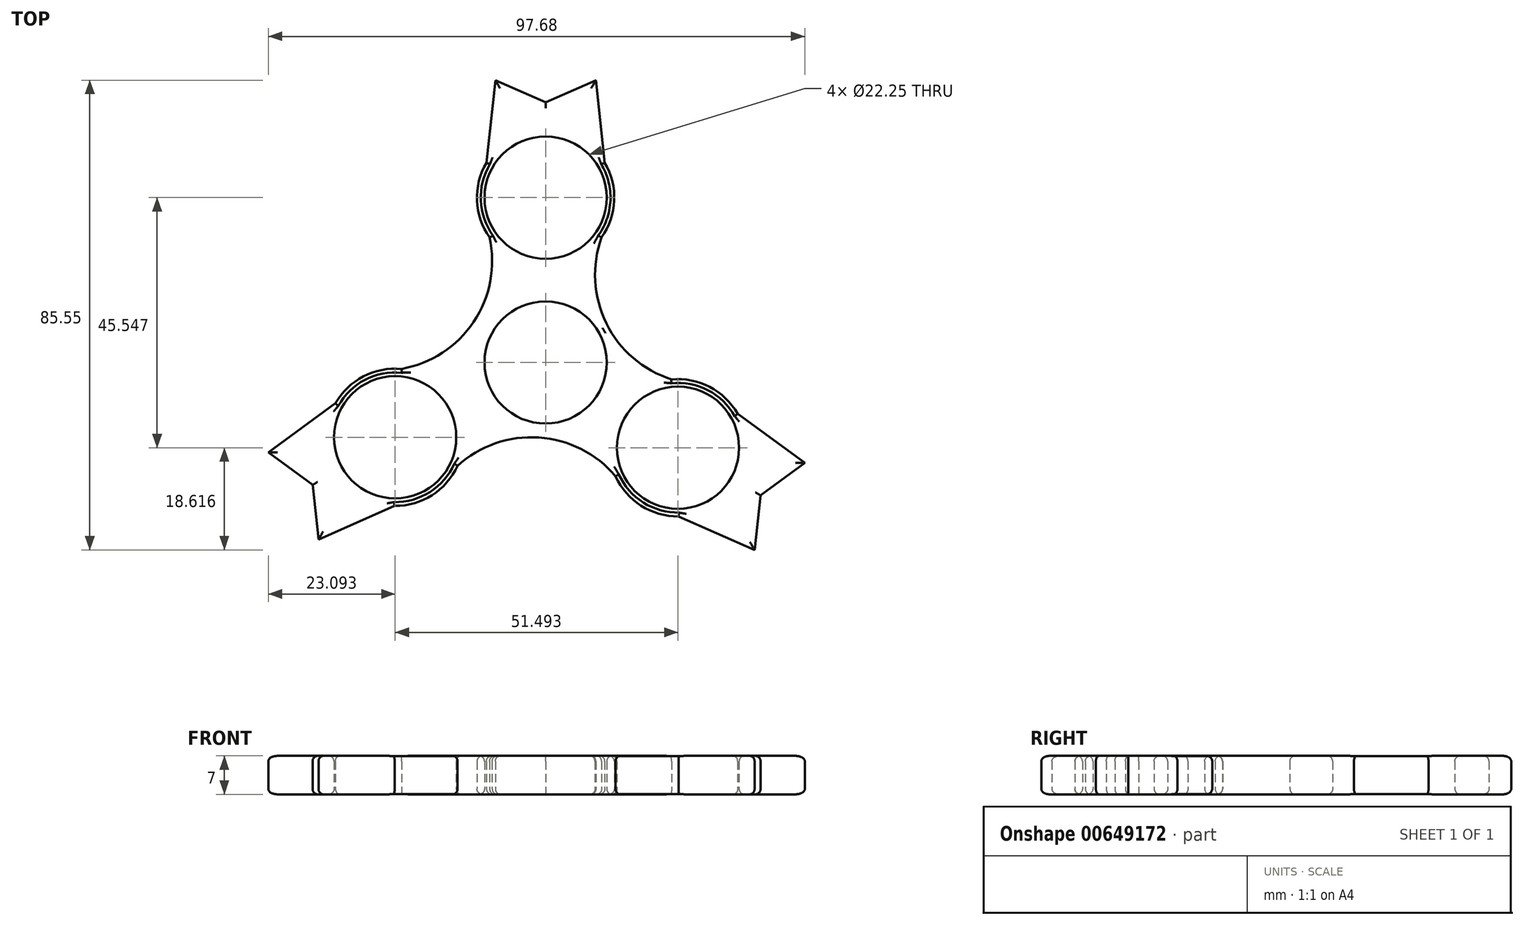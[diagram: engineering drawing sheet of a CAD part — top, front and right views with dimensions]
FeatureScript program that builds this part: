
annotation { "Feature Type Name" : "Feature", "Feature Type Description" : "" }
export const myFeature = defineFeature(function(context is Context, id is Id, definition is map)
    precondition{}
    {
        {
            var Q0;
            Q0=qCreatedBy(makeId("Top.planeOp"),FACE);
            var sketch = newSketch(context, id + "F0", { "sketchPlane" : qUnion([Q0])});
            skCircle(sketch, "E0", {"center": v(0, 0) * mm, "radius": 11.13 * mm});
            skLineSegment(sketch, "E1", {"start": v(32.45, -16.12) * mm, "end": v(32.45, -21.33) * mm, "construction": true});
            skLineSegment(sketch, "E2", {"start": v(-9.15, 36.82) * mm, "end": v(9.15, 36.82) * mm, "construction": true});
            skLineSegment(sketch, "E3", {"start": v(-10.78, 36.35) * mm, "end": v(-9.15, 51.4) * mm});
            skLineSegment(sketch, "E4", {"start": v(-9.15, 51.4) * mm, "end": v(0, 47.38) * mm});
            skLineSegment(sketch, "E5", {"start": v(0, 47.38) * mm, "end": v(9.15, 51.4) * mm});
            skLineSegment(sketch, "E6", {"start": v(9.15, 51.4) * mm, "end": v(10.78, 36.35) * mm});
            skCircle(sketch, "E7", {"center": v(0, 30.02) * mm, "radius": 11.13 * mm});
            skLineSegment(sketch, "E8", {"start": v(-11.33, 31.25) * mm, "end": v(11.33, 31.25) * mm, "construction": true});
            skArc(sketch, "E9", {"start": v(-10.78, 36.35) * mm, "mid": v(-12.49, 29.48) * mm, "end": v(-10.19, 22.78) * mm});
            skCircle(sketch, "E10.1.0", {"center": v(-27.4, -13.62) * mm, "radius": 11.13 * mm});
            skLineSegment(sketch, "E10.1.1", {"start": v(-50.5, -16.38) * mm, "end": v(-38.27, -7.45) * mm});
            skLineSegment(sketch, "E10.1.2", {"start": v(-42.43, -22.3) * mm, "end": v(-50.5, -16.38) * mm});
            skLineSegment(sketch, "E10.1.3", {"start": v(-41.34, -32.24) * mm, "end": v(-42.43, -22.3) * mm});
            skLineSegment(sketch, "E10.1.4", {"start": v(-27.49, -26.12) * mm, "end": v(-41.34, -32.24) * mm});
            skArc(sketch, "E10.1.5", {"start": v(-27.49, -26.12) * mm, "mid": v(-20.68, -24.16) * mm, "end": v(-16.03, -18.82) * mm});
            skCircle(sketch, "E10.2.0", {"center": v(24.1, -15.52) * mm, "radius": 11.13 * mm});
            skLineSegment(sketch, "E10.2.1", {"start": v(38.04, -34.14) * mm, "end": v(24.19, -28.02) * mm});
            skLineSegment(sketch, "E10.2.2", {"start": v(39.13, -24.2) * mm, "end": v(38.04, -34.14) * mm});
            skLineSegment(sketch, "E10.2.3", {"start": v(47.2, -18.29) * mm, "end": v(39.13, -24.2) * mm});
            skLineSegment(sketch, "E10.2.4", {"start": v(34.97, -9.35) * mm, "end": v(47.2, -18.29) * mm});
            skArc(sketch, "E10.2.5", {"start": v(34.97, -9.35) * mm, "mid": v(13.27, -9.27) * mm, "end": v(24.19, -28.02) * mm});
            skPoint(sketch, "E10.center", {"position": v(-1.1, 0.3) * mm});
            skArc(sketch, "E11", {"start": v(12.73, -20.73) * mm, "mid": v(-1.24, -13.65) * mm, "end": v(-16.03, -18.82) * mm});
            skLineSegment(sketch, "E12", {"start": v(-16.03, -18.82) * mm, "end": v(-27.49, -26.12) * mm, "construction": true});
            skLineSegment(sketch, "E13", {"start": v(12.73, -20.73) * mm, "end": v(24.19, -28.02) * mm, "construction": true});
            skArc(sketch, "E14", {"start": v(10.19, 22.78) * mm, "mid": v(11.05, 7.14) * mm, "end": v(22.92, -3.08) * mm});
            skArc(sketch, "E15", {"start": v(-26.22, -1.17) * mm, "mid": v(-13.1, 7.4) * mm, "end": v(-10.19, 22.78) * mm});
            skLineSegment(sketch, "E16", {"start": v(-26.22, -1.17) * mm, "end": v(-38.27, -7.45) * mm, "construction": true});
            skLineSegment(sketch, "E17", {"start": v(-10.3, 25.12) * mm, "end": v(-10.32, 25.88) * mm, "construction": true});
            skLineSegment(sketch, "E18", {"start": v(10.19, 22.78) * mm, "end": v(10.78, 36.35) * mm, "construction": true});
            skLineSegment(sketch, "E19.trimOffspring", {"start": v(-10.56, 31.25) * mm, "end": v(-10.78, 36.35) * mm, "construction": true});
            skArc(sketch, "E20.trimOffspring", {"start": v(10.19, 22.78) * mm, "mid": v(12.49, 29.48) * mm, "end": v(10.78, 36.35) * mm});
            skArc(sketch, "E21.trimOffspring", {"start": v(-26.22, -1.17) * mm, "mid": v(-33.17, -2.53) * mm, "end": v(-38.27, -7.45) * mm});
            skSolve(sketch);
        }
        {
            var Q0;
            Q0=qSketchRegion(id+"F0",true);
            extrude(context, id + "F1", {"entities" : qUnion([Q0]), "depth" : 7 * mm, "offsetDistance" : 25 * mm});
        }
        {
            var Q0;
            Q0=makeQuery(id+"F1.opExtrude","CAP_FACE",FACE,{"disambiguationData":[OSD([sQuery(id+"F0.wireOp",EDGE,"E0"),sQuery(id+"F0.wireOp",EDGE,"E3"),sQuery(id+"F0.wireOp",EDGE,"E4"),sQuery(id+"F0.wireOp",EDGE,"E5"),sQuery(id+"F0.wireOp",EDGE,"E6"),sQuery(id+"F0.wireOp",EDGE,"E7"),sQuery(id+"F0.wireOp",EDGE,"E9"),sQuery(id+"F0.wireOp",EDGE,"E10.1.0"),sQuery(id+"F0.wireOp",EDGE,"E10.1.1"),sQuery(id+"F0.wireOp",EDGE,"E10.1.2"),sQuery(id+"F0.wireOp",EDGE,"E10.1.3"),sQuery(id+"F0.wireOp",EDGE,"E10.1.4"),sQuery(id+"F0.wireOp",EDGE,"E10.1.5"),sQuery(id+"F0.wireOp",EDGE,"E10.2.0"),sQuery(id+"F0.wireOp",EDGE,"E10.2.1"),sQuery(id+"F0.wireOp",EDGE,"E10.2.2"),sQuery(id+"F0.wireOp",EDGE,"E10.2.3"),sQuery(id+"F0.wireOp",EDGE,"E10.2.4"),sQuery(id+"F0.wireOp",EDGE,"E10.2.5"),sQuery(id+"F0.wireOp",EDGE,"E11"),sQuery(id+"F0.wireOp",EDGE,"E14"),sQuery(id+"F0.wireOp",EDGE,"E15"),sQuery(id+"F0.wireOp",EDGE,"E20.trimOffspring"),sQuery(id+"F0.wireOp",EDGE,"E21.trimOffspring")])],"isStart":false});
            fillet(context, id + "F2", {"entities" : qUnion([Q0]), "radius" : 1 * mm, "tangentPropagation" : true, "allowEdgeOverflow" : false});
        }
        {
            var Q0;
            Q0=makeQuery(id+"F1.opExtrude","CAP_FACE",FACE,{"disambiguationData":[OSD([sQuery(id+"F0.wireOp",EDGE,"E0"),sQuery(id+"F0.wireOp",EDGE,"E3"),sQuery(id+"F0.wireOp",EDGE,"E4"),sQuery(id+"F0.wireOp",EDGE,"E5"),sQuery(id+"F0.wireOp",EDGE,"E6"),sQuery(id+"F0.wireOp",EDGE,"E7"),sQuery(id+"F0.wireOp",EDGE,"E9"),sQuery(id+"F0.wireOp",EDGE,"E10.1.0"),sQuery(id+"F0.wireOp",EDGE,"E10.1.1"),sQuery(id+"F0.wireOp",EDGE,"E10.1.2"),sQuery(id+"F0.wireOp",EDGE,"E10.1.3"),sQuery(id+"F0.wireOp",EDGE,"E10.1.4"),sQuery(id+"F0.wireOp",EDGE,"E10.1.5"),sQuery(id+"F0.wireOp",EDGE,"E10.2.0"),sQuery(id+"F0.wireOp",EDGE,"E10.2.1"),sQuery(id+"F0.wireOp",EDGE,"E10.2.2"),sQuery(id+"F0.wireOp",EDGE,"E10.2.3"),sQuery(id+"F0.wireOp",EDGE,"E10.2.4"),sQuery(id+"F0.wireOp",EDGE,"E10.2.5"),sQuery(id+"F0.wireOp",EDGE,"E11"),sQuery(id+"F0.wireOp",EDGE,"E14"),sQuery(id+"F0.wireOp",EDGE,"E15"),sQuery(id+"F0.wireOp",EDGE,"E20.trimOffspring"),sQuery(id+"F0.wireOp",EDGE,"E21.trimOffspring")])],"isStart":true});
            fillet(context, id + "F3", {"entities" : qUnion([Q0]), "radius" : 1 * mm, "tangentPropagation" : true, "allowEdgeOverflow" : false});
        }
    });
